# Revit family: Ballorex_Delta
name_source: partatom
category: Арматура трубопроводов
revit_build: Autodesk Revit 2017 (Build: 20171027_0315(x64)
units: mm (PartAtom-declared; Revit-internal decimal feet)

## family parameters
Всегда вертикально = Да
На основе рабочей плоскости = Нет
Общий = Нет
При загрузке вырезать с полостями = Нет
Размер круглого соединителя = Использовать радиус
Тип детали = Вставляется

## types (19) — shared parameters
ADSK_Единица измерения = шт
ADSK_Завод-изготовитель = Meibes
ADSK_Наименование = Регулятор перепада давления Ballorex Delta с дренажем
Группа модели = Регулятор перепада давления Ballorex Delta с дренажем
Изготовитель = Meibes
Материал полимера = Фильтр_Черный
Материал фитинга = Фильтр_Латунь
Разработчик = ООО ПРОРУБИМ
Разработчик (телефон) = +7(495)649-85-43
Разработчик модели (URL) = http://prorubim.com
zero-valued in all types: ADSK_Масса

## per-type parameters (varying)
| type | ADSK_Код изделия | B | D | D+t | DN | H | H2 | H3 | L | R | S | URL | l1 | l2 | x |
| DN50  dP 60-100 кПА | ME 80589.583 | 77 мм | 138 мм | 54 мм | 50 мм | 286 мм | 25 мм | 24 мм | 135 мм | 25 мм | 90 мм | http://www.meibes.ru | 27 мм | 0 мм | 113 мм |
| DN50 dP 35-75 кПА | ME 80589.582 | 77 мм | 138 мм | 54 мм | 50 мм | 248 мм | 62 мм | 21 мм | 135 мм | 25 мм | 90 мм | http://www.meibes.ru | 27 мм | 0 мм | 113 мм |
| DN40 dP 35-75 кПА | ME 80589.572 | 73 мм | 138 мм | 44 мм | 40 мм | 235 мм | 59 мм | 20 мм | 100 мм | 20 мм | 72 мм |  | 19 мм | 40 мм | 83 мм |
| DN32 dP 20-65 кПА | ME 80589.5282 | 69 мм | 96 мм | 36 мм | 32 мм | 148 мм | 37 мм | 12 мм | 96 мм | 16 мм | 58 мм | http://www.meibes.ru | 19 мм | 32 мм | 80 мм |
| DN25 dP 20-65 кПА | ME 80589.5262 | 65 мм | 96 мм | 29 мм | 25 мм | 146 мм | 37 мм | 12 мм | 84 мм | 13 мм | 45 мм | http://www.meibes.ru | 16 мм | 25 мм | 70 мм |
| DN20 dP 20-65 кПА | ME 80589.5242 | 62 мм | 62 мм | 24 мм | 20 мм | 122 мм | 31 мм | 10 мм | 71 мм | 10 мм | 36 мм | http://www.meibes.ru | 14 мм | 20 мм | 59 мм |
| DN15 dP 20-65 кПА | ME 80589.5222 | 61 мм | 62 мм | 19 мм | 15 мм | 101 мм | 25 мм | 8 мм | 61 мм | 8 мм | 27 мм | http://www.meibes.ru | 12 мм | 15 мм | 51 мм |
| DN50  dP 20-40 кПА | ME 80589.581 | 77 мм | 138 мм | 54 мм | 50 мм | 232 мм | 58 мм | 19 мм | 135 мм | 25 мм | 90 мм | http://www.meibes.ru | 27 мм | 0 мм | 113 мм |
| DN40  dP 20-40 кПА | ME 80589.571 | 73 мм | 138 мм | 44 мм | 40 мм | 220 мм | 55 мм | 18 мм | 100 мм | 20 мм | 72 мм | http://www.meibes.ru | 19 мм | 40 мм | 83 мм |
| DN32  dP 20-40 кПА | ME 80589.528 | 69 мм | 96 мм | 36 мм | 32 мм | 148 мм | 37 мм | 12 мм | 96 мм | 16 мм | 58 мм | http://www.meibes.ru | 19 мм | 32 мм | 80 мм |
| DN25 dP 20-40 кПА | ME 80589.526 | 65 мм | 96 мм | 29 мм | 25 мм | 146 мм | 37 мм | 12 мм | 84 мм | 13 мм | 45 мм | http://www.meibes.ru | 16 мм | 25 мм | 70 мм |
| DN20 dP 20-40 кПА | ME 80589.524 | 62 мм | 62 мм | 24 мм | 20 мм | 122 мм | 31 мм | 10 мм | 71 мм | 10 мм | 36 мм | http://www.meibes.ru | 14 мм | 20 мм | 59 мм |
| DN15 dP 20-40 кПА | ME 80589.522 | 61 мм | 62 мм | 19 мм | 15 мм | 101 мм | 25 мм | 8 мм | 61 мм | 8 мм | 27 мм | http://www.meibes.ru | 12 мм | 15 мм | 51 мм |
| DN50 dP 5-25 кПА | ME 80589.580 | 77 мм | 138 мм | 54 мм | 50 мм | 207 мм | 52 мм | 17 мм | 135 мм | 25 мм | 90 мм | http://www.meibes.ru | 27 мм | 0 мм | 113 мм |
| DN40 dP 5-25 кПА | ME 80589.570 | 73 мм | 138 мм | 44 мм | 40 мм | 194 мм | 49 мм | 16 мм | 100 мм | 20 мм | 72 мм | http://www.meibes.ru | 19 мм | 40 мм | 83 мм |
| DN32 dP 5-25 кПА | ME 80589.527 | 69 мм | 96 мм | 36 мм | 32 мм | 148 мм | 37 мм | 12 мм | 96 мм | 16 мм | 58 мм | http://www.meibes.ru | 19 мм | 32 мм | 80 мм |
| DN25 dP 5-25 кПА | ME 80589.525 | 65 мм | 96 мм | 29 мм | 25 мм | 146 мм | 37 мм | 12 мм | 84 мм | 13 мм | 45 мм | http://www.meibes.ru | 16 мм | 25 мм | 70 мм |
| DN20 dP 5-25 кПА | ME 80589.523 | 62 мм | 62 мм | 24 мм | 20 мм | 122 мм | 31 мм | 10 мм | 71 мм | 10 мм | 36 мм | http://www.meibes.ru | 14 мм | 20 мм | 59 мм |
| DN15 dP 5-25 кПА | ME 80589.521 | 61 мм | 62 мм | 19 мм | 15 мм | 101 мм | 25 мм | 8 мм | 61 мм | 8 мм | 27 мм | http://www.meibes.ru | 12 мм | 15 мм | 51 мм |

note: column(s) folded — value = type name in every type: ADSK_Обозначение
